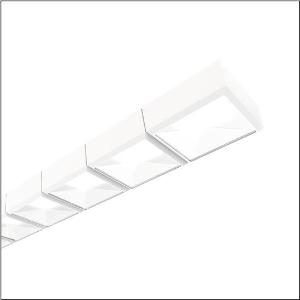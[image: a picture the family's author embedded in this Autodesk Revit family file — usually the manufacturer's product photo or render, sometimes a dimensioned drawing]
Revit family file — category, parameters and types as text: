
# Revit family: scriptus_r__11_5mz313d0twb_9c96
name_source: partatom
category: Lighting Fixtures
units: mm (PartAtom-declared; Revit-internal decimal feet)

## family parameters
Cut with Voids When Loaded = No
Host = Face
Light Source = No
Part Type = Normal
Room Calculation Point = No
Round Connector Dimension = Use Diameter
Shared = No

## types (1)
- --- (1 x LED 3000K+6500K / CRI = 80 (unbekannt), 3390 lm / 3550 lm, 3000K)
    Apparent Load = 107 VA
    CIE Flux Codes = 0 0 0 0 100 / 82 95 99 100 100
    Color Rendering = 80
    Color Temperature = 3000K
    Default Elevation = 1800 mm
    Description = Scriptus® 11, office luminaire, primary optical cover: lenses, CAT 2 (L<= 3000cd/m²), light emission: direct/indirect distribution, primary light characteristic: symmetric, installation type: suspended mounting, LED, rated luminous flux: 13.880lm, luminous efficacy: 126lm/W, light colour: 8tw, colour temperature: 3000..6500K, control gear: ECG DALI, with terminal, 5-pole, mains connection: 230V, AC, 50Hz, rated input power: 110W, LED, control gear: ECG DALI, housing, luminaire housing, of aluminium, traffic white (RAL 9016), length: 2.648mm, width: 114mm, height: 57mm, protection rating (complete): IP20, insulation class (complete): insulation class I (protective earthing), certification: CE, protection symbol: F, permissible operating ambient temperature: <= +25°C, standard: EN 50419, packaging unit: 1 piece
    Height = 57 mm
    Lamp = 1 x LED 3000K+6500K / CRI >= 80 (unbekannt)
    Lamp Light Flux = 3390 lm / 3550 lm
    Lamp count = 1
    Length = 2648 mm
    Luminous efficacy = 130 lm/W
    Manufacturer = Siteco
    ModVariant = No
    Model = 5MZ313D0TWB
    Mounting Place = Ceiling
    Mounting Type = Pendant
    Number of Poles = 1
    OnlyDefault = Yes
    Power Factor = 1
    Product Name = Scriptus® 11
    Product group = office luminaire | ceiling pendant
    ProductGroupID = 902
    Protection Class = Protection class I
    Protection Degree = IP 20
    RLX_Detail_Level = 1
    RLX_Emergency_Light_Flux = 0 lm
    RLX_Emergency_Type = 0
    RLX_Emergency_Type_DB = No
    RlxData = <blob elided: 32049 chars, md5=230a25fd>
    Socket = socket
    Standby Power = 0 W
    System Light Flux = 13880 lm
    System Power = 107 W
    Type Comments = individual setting: colour temperature 6500K
    Type Image = l_1004839.jpg
    URL = http://relux.com
    VarID = @adj_164654
    Voltage = 0 V
    Weight = 0.00 kg
    Width = 114 mm

## geometry (parser evidence)
native form markers: Blend x4, Sweep x19
no freeform markers — native parametric forms only
